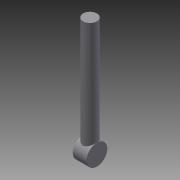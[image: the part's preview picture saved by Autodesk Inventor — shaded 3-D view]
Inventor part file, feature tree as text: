
AUTODESK INVENTOR PART (.ipt)
format: ipt  version: 2014 (Build 180170000, 170)  size: 79,360 bytes
history: native  units: in
note: dims shown in document units (in); Inventor stores cm internally (conversion verified against a paired STEP export)
features: extrude x2, sketch x2
ambient origin geometry x8: Origin, YZ Plane, XZ Plane, XY Plane, X Axis, Y Axis, Z Axis, Center Point
bodies: Solid1 (feature_tree)
feature tree (4):
  extrude  "Extrusion1"  Depth=4.0in TaperAngle=0.0deg
  extrude  "Extrusion3"  Depth=0.1779in
  sketch  "Sketch1"  dims[d0=0.5in d1=4.0in d2=0.0in]
  sketch  "Sketch3"  dims[d6=0.75in d7=0.1779in d9=0.3068in d10=0.5in d11=0.0in]
